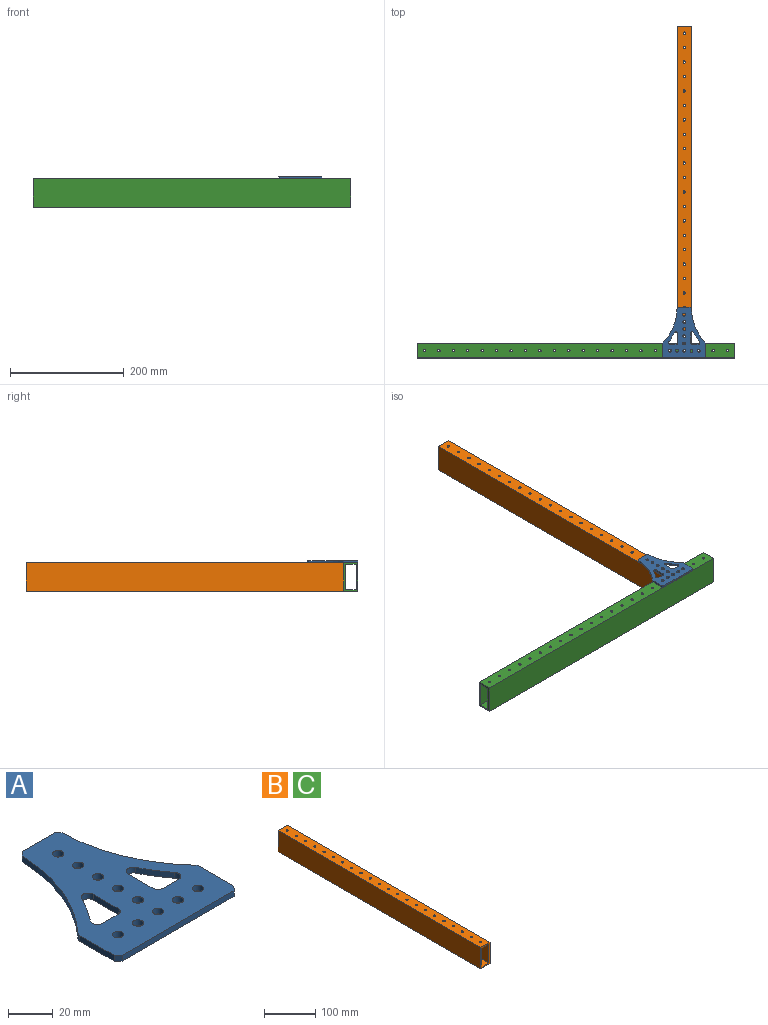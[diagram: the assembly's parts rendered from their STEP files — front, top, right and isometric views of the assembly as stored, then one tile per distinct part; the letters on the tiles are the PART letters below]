
ASSEMBLY  parts=3 mates=5
PART A: 36 faces, bbox 76.2x88.9x3.2 mm
  f0: plane 9.93x3.18mm, normal (0,1,0), area 31.5mm2, adj f12,f13,f24,f26
  f1: plane 15.71x3.18mm, normal (1,0,0), area 49.9mm2, adj f12,f13,f24,f25
  f2: plane 71.12x3.18mm, normal (0,-1,0), area 225.8mm2, adj f12,f13,f18,f20
  f3: plane 21.85x3.18mm, normal (1,0,0), area 69.4mm2, adj f12,f13,f19,f20
  f4: cylinder r=92.08mm len=60.3mm, axis (0,0,-1), area 211.5mm2, adj f12,f13,f15,f19
  f5: plane 20.39x3.18mm, normal (0,1,0), area 64.7mm2, adj f12,f13,f15,f17
  f6: cylinder r=92.08mm len=60.3mm, axis (0,0,-1), area 211.5mm2, adj f12,f13,f16,f17
  f7: cylinder r=98.42mm len=15.22mm, axis (0,0,-1), area 57.2mm2, adj f12,f13,f21,f23
  f8: plane 15.71x3.18mm, normal (-1,0,0), area 49.9mm2, adj f12,f13,f21,f22
  f9: plane 21.85x3.18mm, normal (-1,0,0), area 69.4mm2, adj f12,f13,f16,f18
  f10: plane 9.93x3.18mm, normal (0,1,0), area 31.5mm2, adj f12,f13,f22,f23
  f11: cylinder r=98.42mm len=15.22mm, axis (0,0,-1), area 57.2mm2, adj f12,f13,f25,f26
  f12: plane 88.9x76.2mm, normal (0,0,1), area 3848.5mm2, adj f0,f1,f2,f3,f4,f5,f6,f7
  f13: plane 88.9x76.2mm, normal (0,0,-1), area 3848.5mm2, adj f0,f1,f2,f3,f4,f5,f6,f7
  f14: cylinder r=2.55mm len=5.11mm, axis (0,0,1), area 50.9mm2, adj f12,f13
  f15: plane 3.18x2.54mm, normal (0.7,0.72,0), area 11.3mm2, adj f4,f5,f12,f13
  f16: plane 3.18x1.73mm, normal (-0.93,0.37,0), area 5.9mm2, adj f6,f9,f12,f13
  f17: plane 3.18x2.54mm, normal (-0.7,0.72,0), area 11.3mm2, adj f5,f6,f12,f13
  f18: plane 3.18x2.54mm, normal (-0.71,-0.71,0), area 11.4mm2, adj f2,f9,f12,f13
  f19: plane 3.18x1.73mm, normal (0.93,0.37,0), area 5.9mm2, adj f3,f4,f12,f13
  f20: plane 3.18x2.54mm, normal (0.71,-0.71,0), area 11.4mm2, adj f2,f3,f12,f13
  f21: cylinder r=3.17mm len=6mm, axis (0,0,-1), area 26.9mm2, adj f7,f8,f12,f13
  f22: cylinder r=3.17mm len=3.18mm, axis (0,0,1), area 15.8mm2, adj f8,f10,f12,f13
  f23: cylinder r=3.17mm len=5.11mm, axis (0,0,-1), area 22.4mm2, adj f7,f10,f12,f13
  f24: cylinder r=3.17mm len=3.18mm, axis (0,0,1), area 15.8mm2, adj f0,f1,f12,f13
  f25: cylinder r=3.17mm len=6mm, axis (0,0,-1), area 26.9mm2, adj f1,f11,f12,f13
  f26: cylinder r=3.17mm len=5.11mm, axis (0,0,-1), area 22.4mm2, adj f0,f11,f12,f13
  f27: cylinder r=2.55mm len=5.11mm, axis (0,0,1), area 50.9mm2, adj f12,f13
  f28: cylinder r=2.55mm len=5.11mm, axis (0,0,1), area 50.9mm2, adj f12,f13
  f29: cylinder r=2.55mm len=5.11mm, axis (0,0,1), area 50.9mm2, adj f12,f13
  f30: cylinder r=2.55mm len=5.11mm, axis (0,0,1), area 50.9mm2, adj f12,f13
  f31: cylinder r=2.55mm len=5.11mm, axis (0,0,1), area 50.9mm2, adj f12,f13
  f32: cylinder r=2.55mm len=5.11mm, axis (0,0,1), area 50.9mm2, adj f12,f13
  f33: cylinder r=2.55mm len=5.11mm, axis (0,0,1), area 50.9mm2, adj f12,f13
  f34: cylinder r=2.55mm len=5.11mm, axis (0,0,1), area 50.9mm2, adj f12,f13
  f35: cylinder r=2.55mm len=5.11mm, axis (0,0,1), area 50.9mm2, adj f12,f13
PART B: 54 faces, bbox 25.4x558.8x50.8 mm
  f0: plane 558.8x19.05mm, normal (0,0,-1), area 10324.9mm2, adj f1,f7,f8,f9,f11,f13,f15,f17
  f1: plane 558.8x44.45mm, normal (-1,0,0), area 24838.7mm2, adj f0,f2,f8,f9
  f2: plane 558.8x19.05mm, normal (0,0,1), area 10324.9mm2, adj f1,f7,f8,f9,f10,f12,f14,f16
  f3: plane 558.8x50.8mm, normal (1,0,0), area 28387mm2, adj f4,f6,f8,f9
  f4: plane 558.8x25.4mm, normal (0,0,1), area 13873.2mm2, adj f3,f5,f8,f9,f11,f13,f15,f17
  f5: plane 558.8x50.8mm, normal (-1,0,0), area 28387mm2, adj f4,f6,f8,f9
  f6: plane 558.8x25.4mm, normal (0,0,-1), area 13873.2mm2, adj f3,f5,f8,f9,f10,f12,f14,f16
  f7: plane 558.8x44.45mm, normal (1,0,0), area 24838.7mm2, adj f0,f2,f8,f9
  f8: plane 50.8x25.4mm, normal (0,-1,0), area 443.5mm2, adj f0,f1,f2,f3,f4,f5,f6,f7
  f9: plane 50.8x25.4mm, normal (0,1,0), area 443.5mm2, adj f0,f1,f2,f3,f4,f5,f6,f7
  f10: cylinder r=2.15mm len=4.31mm, axis (0,0,1), area 42.9mm2, adj f2,f6
  f11: cylinder r=2.15mm len=4.31mm, axis (0,0,1), area 42.9mm2, adj f0,f4
  f12: cylinder r=2.15mm len=4.31mm, axis (0,0,1), area 42.9mm2, adj f2,f6
  f13: cylinder r=2.15mm len=4.31mm, axis (0,0,1), area 42.9mm2, adj f0,f4
  f14: cylinder r=2.15mm len=4.31mm, axis (0,0,1), area 42.9mm2, adj f2,f6
  f15: cylinder r=2.15mm len=4.31mm, axis (0,0,1), area 42.9mm2, adj f0,f4
  f16: cylinder r=2.15mm len=4.31mm, axis (0,0,1), area 42.9mm2, adj f2,f6
  f17: cylinder r=2.15mm len=4.31mm, axis (0,0,1), area 42.9mm2, adj f0,f4
  f18: cylinder r=2.15mm len=4.31mm, axis (0,0,1), area 42.9mm2, adj f2,f6
  f19: cylinder r=2.15mm len=4.31mm, axis (0,0,1), area 42.9mm2, adj f0,f4
  f20: cylinder r=2.15mm len=4.31mm, axis (0,0,1), area 42.9mm2, adj f2,f6
  f21: cylinder r=2.15mm len=4.31mm, axis (0,0,1), area 42.9mm2, adj f0,f4
  f22: cylinder r=2.15mm len=4.31mm, axis (0,0,1), area 42.9mm2, adj f2,f6
  f23: cylinder r=2.15mm len=4.31mm, axis (0,0,1), area 42.9mm2, adj f0,f4
  f24: cylinder r=2.15mm len=4.31mm, axis (0,0,1), area 42.9mm2, adj f2,f6
  f25: cylinder r=2.15mm len=4.31mm, axis (0,0,1), area 42.9mm2, adj f0,f4
  f26: cylinder r=2.15mm len=4.31mm, axis (0,0,1), area 42.9mm2, adj f2,f6
  f27: cylinder r=2.15mm len=4.31mm, axis (0,0,1), area 42.9mm2, adj f0,f4
  f28: cylinder r=2.15mm len=4.31mm, axis (0,0,1), area 42.9mm2, adj f2,f6
  f29: cylinder r=2.15mm len=4.31mm, axis (0,0,1), area 42.9mm2, adj f0,f4
  f30: cylinder r=2.15mm len=4.31mm, axis (0,0,1), area 42.9mm2, adj f2,f6
  f31: cylinder r=2.15mm len=4.31mm, axis (0,0,1), area 42.9mm2, adj f0,f4
  f32: cylinder r=2.15mm len=4.31mm, axis (0,0,1), area 42.9mm2, adj f2,f6
  f33: cylinder r=2.15mm len=4.31mm, axis (0,0,1), area 42.9mm2, adj f0,f4
  f34: cylinder r=2.15mm len=4.31mm, axis (0,0,1), area 42.9mm2, adj f2,f6
  f35: cylinder r=2.15mm len=4.31mm, axis (0,0,1), area 42.9mm2, adj f0,f4
  f36: cylinder r=2.15mm len=4.31mm, axis (0,0,1), area 42.9mm2, adj f2,f6
  f37: cylinder r=2.15mm len=4.31mm, axis (0,0,1), area 42.9mm2, adj f0,f4
  f38: cylinder r=2.15mm len=4.31mm, axis (0,0,1), area 42.9mm2, adj f2,f6
  f39: cylinder r=2.15mm len=4.31mm, axis (0,0,1), area 42.9mm2, adj f0,f4
  f40: cylinder r=2.15mm len=4.31mm, axis (0,0,1), area 42.9mm2, adj f2,f6
  f41: cylinder r=2.15mm len=4.31mm, axis (0,0,1), area 42.9mm2, adj f0,f4
  f42: cylinder r=2.15mm len=4.31mm, axis (0,0,1), area 42.9mm2, adj f2,f6
  f43: cylinder r=2.15mm len=4.31mm, axis (0,0,1), area 42.9mm2, adj f0,f4
  f44: cylinder r=2.15mm len=4.31mm, axis (0,0,1), area 42.9mm2, adj f2,f6
  f45: cylinder r=2.15mm len=4.31mm, axis (0,0,1), area 42.9mm2, adj f0,f4
  f46: cylinder r=2.15mm len=4.31mm, axis (0,0,1), area 42.9mm2, adj f2,f6
  f47: cylinder r=2.15mm len=4.31mm, axis (0,0,1), area 42.9mm2, adj f0,f4
  f48: cylinder r=2.15mm len=4.31mm, axis (0,0,1), area 42.9mm2, adj f2,f6
  f49: cylinder r=2.15mm len=4.31mm, axis (0,0,1), area 42.9mm2, adj f0,f4
  f50: cylinder r=2.15mm len=4.31mm, axis (0,0,1), area 42.9mm2, adj f2,f6
  f51: cylinder r=2.15mm len=4.31mm, axis (0,0,1), area 42.9mm2, adj f0,f4
  f52: cylinder r=2.15mm len=4.31mm, axis (0,0,1), area 42.9mm2, adj f2,f6
  f53: cylinder r=2.15mm len=4.31mm, axis (0,0,1), area 42.9mm2, adj f0,f4
PART C: same geometry as B
PLACE A rot(axis=(0,1,0),180deg) t=(120.35,-312.42,31.28)mm
PLACE B t=(120.35,-20.32,4.29)mm fixed
PLACE C rot(axis=(0,0,-1),90deg) t=(-70.15,-312.42,4.29)mm
MATE planar A.f12 <-> B.f4  axis (0,0,-1) through (134.64,-301.3,29.69)mm
MATE cylindrical A.f14 <-> C.f16  axis (0,0,-1) through (120.35,-312.42,29.69)mm
MATE parallel C.f3 <-> B.f8  axis (0,-1,0) through (-70.15,-325.12,4.29)mm
MATE planar B.f8 <-> C.f5  axis (0,-1,0) through (129.87,-299.72,4.29)mm
MATE cylindrical B.f52 <-> A.f28  axis (0,0,1) through (120.35,-287.02,29.69)mm
